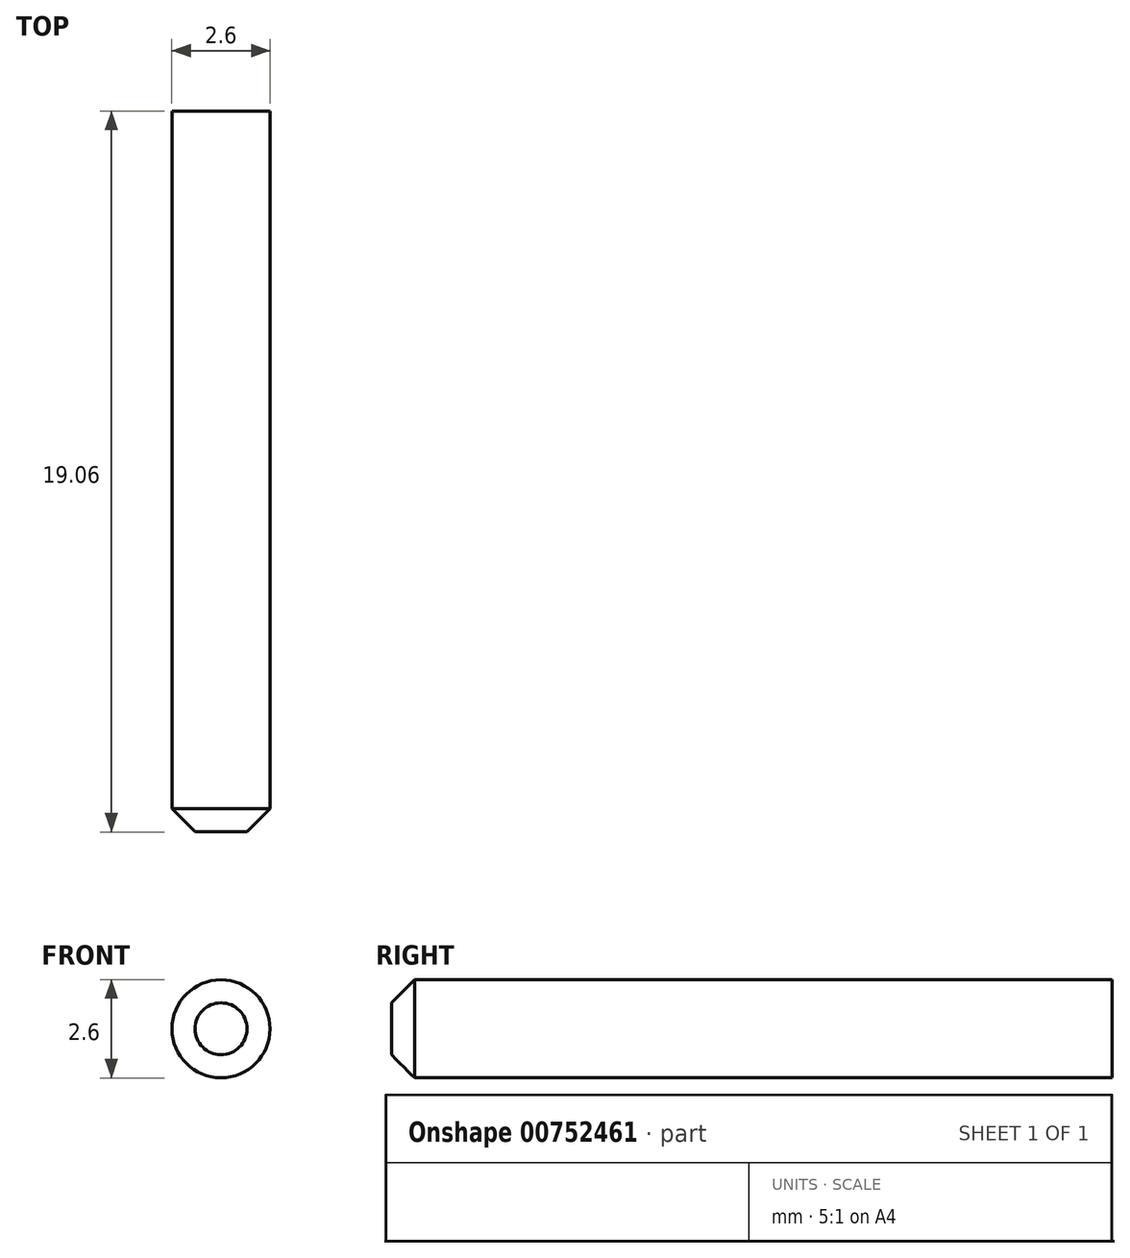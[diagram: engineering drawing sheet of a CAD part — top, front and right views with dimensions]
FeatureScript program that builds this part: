
annotation { "Feature Type Name" : "Feature", "Feature Type Description" : "" }
export const myFeature = defineFeature(function(context is Context, id is Id, definition is map)
    precondition{}
    {
        {
            var Q0;
            Q0=qCreatedBy(makeId("Front.planeOp"),FACE);
            var sketch = newSketch(context, id + "F0", { "sketchPlane" : qUnion([Q0])});
            skCircle(sketch, "E0", {"center": v(0, 0) * mm, "radius": 1.3 * mm});
            skSolve(sketch);
        }
        {
            var Q0;
            Q0 = qSketchRegion(id + "F0", true);
            extrude(context, id + "F1", {"entities" : qUnion([Q0]), "endBound" : BoundingType.SYMMETRIC, "depth" : 19.05 * mm, "offsetDistance" : 25.4 * mm});
        }
        {
            var Q0;
            Q0=makeQuery(id+"F1.opExtrude","CAP_EDGE",EDGE,{"disambiguationData":[OSD([sQuery(id+"F0.wireOp",EDGE,"E0")])],"isStart":false});
            chamfer(context, id + "F2", {"entities" : qUnion([Q0]), "width" : 0.6 * mm, "tangentPropagation" : true});
        }
    });
